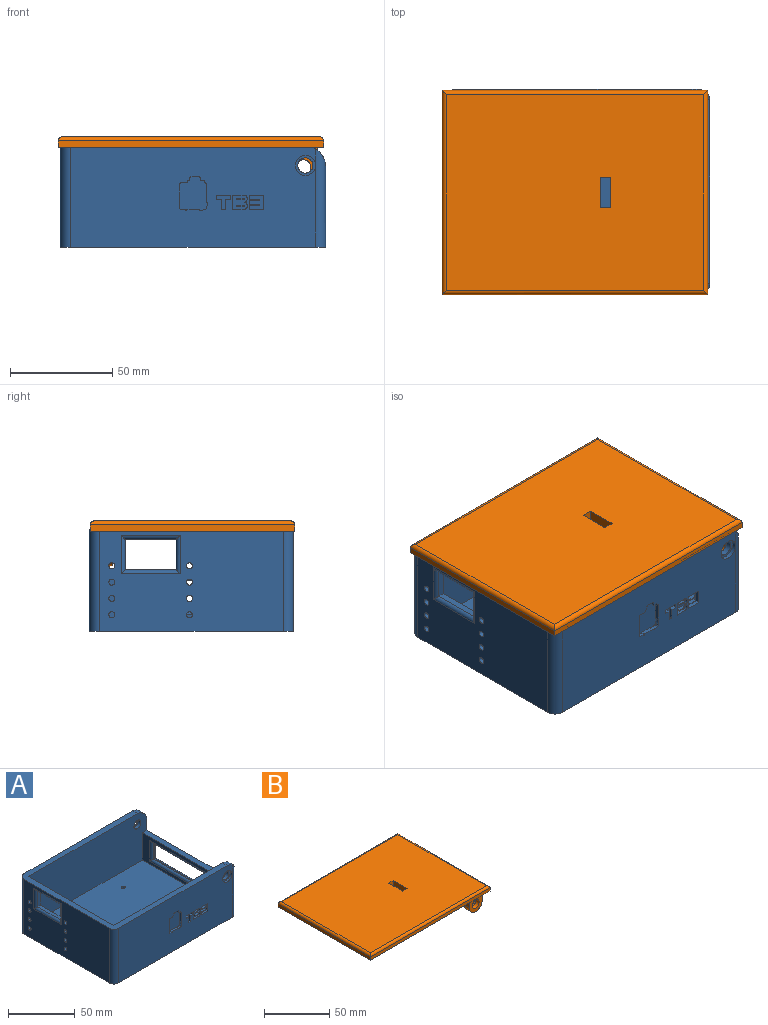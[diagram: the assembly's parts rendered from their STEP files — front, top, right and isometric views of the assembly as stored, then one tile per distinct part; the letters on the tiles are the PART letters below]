
ASSEMBLY  parts=2 mates=1
PART A: 193 faces, bbox 130x100x50 mm
  f0: plane 120x50mm, normal (0,-1,0), area 5613.6mm2, adj f12,f21,f23,f42,f44,f47,f50,f124
  f1: cylinder r=1.5mm len=3mm, axis (-1,0,0), area 28.3mm2, adj f9,f111
  f2: cylinder r=1.5mm len=3mm, axis (-1,0,0), area 28.3mm2, adj f9,f104
  f3: cylinder r=1.5mm len=3mm, axis (-1,0,0), area 28.3mm2, adj f9,f97
  f4: cylinder r=1.5mm len=3mm, axis (-1,0,0), area 28.3mm2, adj f9,f90
  f5: cylinder r=1.5mm len=3mm, axis (-1,0,0), area 28.3mm2, adj f9,f83
  f6: cylinder r=1.5mm len=3mm, axis (-1,0,0), area 28.3mm2, adj f9,f76
  f7: cylinder r=1.5mm len=3mm, axis (-1,0,0), area 28.3mm2, adj f9,f69
  f8: cylinder r=1.5mm len=3mm, axis (-1,0,0), area 28.3mm2, adj f9,f62
  f9: plane 90x50mm, normal (-1,0,0), area 3892.5mm2, adj f1,f2,f3,f4,f5,f6,f7,f8
  f10: plane 90x45mm, normal (1,0,0), area 3502.5mm2, adj f21,f24,f25,f26,f52,f53,f54,f55
  f11: plane 0.67x0.05mm, normal (0,0,1), area 0mm2, adj f12,f24,f47
  f12: cylinder r=11mm len=9.95mm, axis (0,-1,0), area 60.3mm2, adj f0,f11,f24,f42,f47
  f13: cylinder r=3.75mm len=7.5mm, axis (0,-1,0), area 70.7mm2, adj f25,f45
  f14: cylinder r=3.75mm len=7.5mm, axis (0,-1,0), area 70.7mm2, adj f24,f43
  f15: plane 90x25mm, normal (-1,0,0), area 844mm2, adj f24,f25,f26,f51,f116,f117,f118,f119
  f16: cylinder r=1.5mm len=3mm, axis (0,0,1), area 23.6mm2, adj f26,f38
  f17: cylinder r=1.5mm len=3mm, axis (0,0,1), area 23.6mm2, adj f26,f36
  f18: cylinder r=1.5mm len=3mm, axis (0,0,1), area 23.6mm2, adj f26,f34
  f19: cylinder r=1.5mm len=3mm, axis (0,0,1), area 23.6mm2, adj f26,f32
  f20: plane 90x30mm, normal (1,0,0), area 1294mm2, adj f23,f47,f48,f51,f112,f113,f114,f115
  f21: plane 120x100mm, normal (0,0,1), area 1639.3mm2, adj f0,f9,f10,f22,f24,f25,f40,f42
  f22: plane 120x50mm, normal (0,1,0), area 5918mm2, adj f21,f23,f40,f41,f46,f48,f49
  f23: plane 130x100mm, normal (0,0,-1), area 12900mm2, adj f0,f9,f20,f22,f31,f33,f35,f37
  f24: plane 125x45mm, normal (0,1,0), area 5429.9mm2, adj f10,f11,f12,f14,f15,f21,f26,f42
  f25: plane 125x45mm, normal (0,-1,0), area 5429.9mm2, adj f10,f13,f15,f21,f26,f39,f40,f41
  f26: plane 120x90mm, normal (0,0,1), area 10771.7mm2, adj f10,f15,f16,f17,f18,f19,f24,f25
  f27: plane 70x1mm, normal (0,0,1), area 70mm2, adj f28,f30,f115,f116
  f28: plane 15x1mm, normal (0,1,0), area 15mm2, adj f27,f29,f113,f117
  f29: plane 70x1mm, normal (0,0,-1), area 70mm2, adj f28,f30,f112,f119
  f30: plane 15x1mm, normal (0,-1,0), area 15mm2, adj f27,f29,f114,f118
  f31: cylinder r=2.5mm len=5mm, axis (0,0,-1), area 39.3mm2, adj f23,f32
  f32: plane 5x5mm, normal (0,0,-1), area 12.6mm2, adj f19,f31
  f33: cylinder r=2.5mm len=5mm, axis (0,0,-1), area 39.3mm2, adj f23,f34
  f34: plane 5x5mm, normal (0,0,-1), area 12.6mm2, adj f18,f33
  f35: cylinder r=2.5mm len=5mm, axis (0,0,-1), area 39.3mm2, adj f23,f36
  f36: plane 5x5mm, normal (0,0,-1), area 12.6mm2, adj f17,f35
  f37: cylinder r=2.5mm len=5mm, axis (0,0,-1), area 39.3mm2, adj f23,f38
  f38: plane 5x5mm, normal (0,0,-1), area 12.6mm2, adj f16,f37
  f39: plane 0.67x0.05mm, normal (0,0,1), area 0mm2, adj f25,f41,f48
  f40: plane 5x0.05mm, normal (1,0,0), area 0.2mm2, adj f21,f22,f25,f41
  f41: cylinder r=11mm len=9.95mm, axis (0,-1,0), area 60.3mm2, adj f22,f25,f39,f40,f48
  f42: plane 5x0.05mm, normal (1,0,0), area 0.2mm2, adj f0,f12,f21,f24
  f43: plane 10x10mm, normal (0,-1,0), area 34.4mm2, adj f14,f44
  f44: cylinder r=5mm len=10mm, axis (0,-1,0), area 62.8mm2, adj f0,f43
  f45: plane 10x10mm, normal (0,1,0), area 34.4mm2, adj f13,f46
  f46: cylinder r=5mm len=10mm, axis (0,1,0), area 62.8mm2, adj f22,f45
  f47: cylinder r=5mm len=48.22mm, axis (0,0,1), area 347.4mm2, adj f0,f11,f12,f20,f23,f24
  f48: cylinder r=5mm len=48.22mm, axis (0,0,-1), area 347.4mm2, adj f20,f22,f23,f25,f39,f41
  f49: cylinder r=5mm len=50mm, axis (0,0,1), area 392.7mm2, adj f9,f21,f22,f23
  f50: cylinder r=5mm len=50mm, axis (0,0,-1), area 392.7mm2, adj f0,f9,f21,f23
  f51: plane 90x5mm, normal (0,0,1), area 450mm2, adj f15,f20,f24,f25
  f52: plane 25x3mm, normal (0,0,1), area 75mm2, adj f10,f53,f55,f121
  f53: plane 15x3mm, normal (0,1,0), area 45mm2, adj f10,f52,f54,f120
  f54: plane 25x3mm, normal (0,0,-1), area 75mm2, adj f10,f53,f55,f122
  f55: plane 15x3mm, normal (0,-1,0), area 45mm2, adj f10,f52,f54,f123
  f56: plane 2.89x2mm, normal (0,0,1), area 5.8mm2, adj f10,f57,f61,f62
  f57: plane 2.5x2mm, normal (0,-0.87,0.5), area 5.8mm2, adj f10,f56,f58,f62
  f58: plane 2.5x2mm, normal (0,-0.87,-0.5), area 5.8mm2, adj f10,f57,f59,f62
  f59: plane 2.89x2mm, normal (0,0,-1), area 5.8mm2, adj f10,f58,f60,f62
  f60: plane 2.5x2mm, normal (0,0.87,-0.5), area 5.8mm2, adj f10,f59,f61,f62
  f61: plane 2.5x2mm, normal (0,0.87,0.5), area 5.8mm2, adj f10,f56,f60,f62
  f62: plane 5.77x5mm, normal (1,0,0), area 14.6mm2, adj f8,f56,f57,f58,f59,f60,f61
  f63: plane 2.89x2mm, normal (0,0,1), area 5.8mm2, adj f10,f64,f68,f69
  f64: plane 2.5x2mm, normal (0,-0.87,0.5), area 5.8mm2, adj f10,f63,f65,f69
  f65: plane 2.5x2mm, normal (0,-0.87,-0.5), area 5.8mm2, adj f10,f64,f66,f69
  f66: plane 2.89x2mm, normal (0,0,-1), area 5.8mm2, adj f10,f65,f67,f69
  f67: plane 2.5x2mm, normal (0,0.87,-0.5), area 5.8mm2, adj f10,f66,f68,f69
  f68: plane 2.5x2mm, normal (0,0.87,0.5), area 5.8mm2, adj f10,f63,f67,f69
  f69: plane 5.77x5mm, normal (1,0,0), area 14.6mm2, adj f7,f63,f64,f65,f66,f67,f68
  f70: plane 2.5x2mm, normal (0,0.87,-0.5), area 5.8mm2, adj f10,f71,f75,f76
  f71: plane 2.5x2mm, normal (0,0.87,0.5), area 5.8mm2, adj f10,f70,f72,f76
  f72: plane 2.89x2mm, normal (0,0,1), area 5.8mm2, adj f10,f71,f73,f76
  f73: plane 2.5x2mm, normal (0,-0.87,0.5), area 5.8mm2, adj f10,f72,f74,f76
  f74: plane 2.5x2mm, normal (0,-0.87,-0.5), area 5.8mm2, adj f10,f73,f75,f76
  f75: plane 2.89x2mm, normal (0,0,-1), area 5.8mm2, adj f10,f70,f74,f76
  f76: plane 5.77x5mm, normal (1,0,0), area 14.6mm2, adj f6,f70,f71,f72,f73,f74,f75
  f77: plane 2.5x2mm, normal (0,-0.5,0.87), area 5.8mm2, adj f10,f78,f82,f83
  f78: plane 2.89x2mm, normal (0,-1,0), area 5.8mm2, adj f10,f77,f79,f83
  f79: plane 2.5x2mm, normal (0,-0.5,-0.87), area 5.8mm2, adj f10,f78,f80,f83
  f80: plane 2.5x2mm, normal (0,0.5,-0.87), area 5.8mm2, adj f10,f79,f81,f83
  f81: plane 2.89x2mm, normal (0,1,0), area 5.8mm2, adj f10,f80,f82,f83
  f82: plane 2.5x2mm, normal (0,0.5,0.87), area 5.8mm2, adj f10,f77,f81,f83
  f83: plane 5.77x5mm, normal (1,0,0), area 14.6mm2, adj f5,f77,f78,f79,f80,f81,f82
  f84: plane 2.5x2mm, normal (0,0.5,-0.87), area 5.8mm2, adj f10,f85,f89,f90
  f85: plane 2.89x2mm, normal (0,1,0), area 5.8mm2, adj f10,f84,f86,f90
  f86: plane 2.5x2mm, normal (0,0.5,0.87), area 5.8mm2, adj f10,f85,f87,f90
  f87: plane 2.5x2mm, normal (0,-0.5,0.87), area 5.8mm2, adj f10,f86,f88,f90
  f88: plane 2.89x2mm, normal (0,-1,0), area 5.8mm2, adj f10,f87,f89,f90
  f89: plane 2.5x2mm, normal (0,-0.5,-0.87), area 5.8mm2, adj f10,f84,f88,f90
  f90: plane 5.77x5mm, normal (1,0,0), area 14.6mm2, adj f4,f84,f85,f86,f87,f88,f89
  f91: plane 2.5x2mm, normal (0,0.5,-0.87), area 5.8mm2, adj f10,f92,f96,f97
  f92: plane 2.89x2mm, normal (0,1,0), area 5.8mm2, adj f10,f91,f93,f97
  f93: plane 2.5x2mm, normal (0,0.5,0.87), area 5.8mm2, adj f10,f92,f94,f97
  f94: plane 2.5x2mm, normal (0,-0.5,0.87), area 5.8mm2, adj f10,f93,f95,f97
  f95: plane 2.89x2mm, normal (0,-1,0), area 5.8mm2, adj f10,f94,f96,f97
  f96: plane 2.5x2mm, normal (0,-0.5,-0.87), area 5.8mm2, adj f10,f91,f95,f97
  f97: plane 5.77x5mm, normal (1,0,0), area 14.6mm2, adj f3,f91,f92,f93,f94,f95,f96
  f98: plane 2.46x2mm, normal (0,0.5,-0.87), area 5.7mm2, adj f10,f99,f103,f104
  f99: plane 2.84x2mm, normal (0,1,0), area 5.7mm2, adj f10,f98,f100,f104
  f100: plane 2.46x2mm, normal (0,0.5,0.87), area 5.7mm2, adj f10,f99,f101,f104
  f101: plane 2.46x2mm, normal (0,-0.5,0.87), area 5.7mm2, adj f10,f100,f102,f104
  f102: plane 2.84x2mm, normal (0,-1,0), area 5.7mm2, adj f10,f101,f103,f104
  f103: plane 2.46x2mm, normal (0,-0.5,-0.87), area 5.7mm2, adj f10,f98,f102,f104
  f104: plane 5.68x4.92mm, normal (1,0,0), area 13.9mm2, adj f2,f98,f99,f100,f101,f102,f103
  f105: plane 2.5x2mm, normal (0,0.5,-0.87), area 5.8mm2, adj f10,f106,f110,f111
  f106: plane 2.89x2mm, normal (0,1,0), area 5.8mm2, adj f10,f105,f107,f111
  f107: plane 2.5x2mm, normal (0,0.5,0.87), area 5.8mm2, adj f10,f106,f108,f111
  f108: plane 2.5x2mm, normal (0,-0.5,0.87), area 5.8mm2, adj f10,f107,f109,f111
  f109: plane 2.89x2mm, normal (0,-1,0), area 5.8mm2, adj f10,f108,f110,f111
  f110: plane 2.5x2mm, normal (0,-0.5,-0.87), area 5.8mm2, adj f10,f105,f109,f111
  f111: plane 5.77x5mm, normal (1,0,0), area 14.6mm2, adj f1,f105,f106,f107,f108,f109,f110
  f112: cylinder r=2mm len=74mm, axis (0,1,0), area 224.5mm2, adj f20,f29,f113,f114
  f113: cylinder r=2mm len=19mm, axis (0,0,1), area 51.7mm2, adj f20,f28,f112,f115
  f114: cylinder r=2mm len=19mm, axis (0,0,-1), area 51.7mm2, adj f20,f30,f112,f115
  f115: cylinder r=2mm len=74mm, axis (0,-1,0), area 224.5mm2, adj f20,f27,f113,f114
  f116: cylinder r=2mm len=74mm, axis (0,-1,0), area 224.5mm2, adj f15,f27,f117,f118
  f117: cylinder r=2mm len=19mm, axis (0,0,1), area 51.7mm2, adj f15,f28,f116,f119
  f118: cylinder r=2mm len=19mm, axis (0,0,-1), area 51.7mm2, adj f15,f30,f116,f119
  f119: cylinder r=2mm len=74mm, axis (0,1,0), area 224.5mm2, adj f15,f29,f117,f118
  f120: cylinder r=2mm len=19mm, axis (0,0,-1), area 51.7mm2, adj f9,f53,f121,f122
  f121: cylinder r=2mm len=29mm, axis (0,1,0), area 83.1mm2, adj f9,f52,f120,f123
  f122: cylinder r=2mm len=29mm, axis (0,-1,0), area 83.1mm2, adj f9,f54,f120,f123
  f123: cylinder r=2mm len=19mm, axis (0,0,1), area 51.7mm2, adj f9,f55,f121,f122
  f124: plane 7x2mm, normal (0,0,-1), area 14mm2, adj f0,f125,f131,f132
  f125: plane 2x2mm, normal (1,0,0), area 4mm2, adj f0,f124,f126,f132
  f126: plane 2.5x2mm, normal (0,0,1), area 5mm2, adj f0,f125,f127,f132
  f127: plane 5x2mm, normal (1,0,0), area 10mm2, adj f0,f126,f128,f132
  f128: plane 2x2mm, normal (0,0,1), area 4mm2, adj f0,f127,f129,f132
  f129: plane 5x2mm, normal (-1,0,0), area 10mm2, adj f0,f128,f130,f132
  f130: plane 2.5x2mm, normal (0,0,1), area 5mm2, adj f0,f129,f131,f132
  f131: plane 2x2mm, normal (-1,0,0), area 4mm2, adj f0,f124,f130,f132
  f132: plane 7x7mm, normal (0,-1,0), area 24mm2, adj f124,f125,f126,f127,f128,f129,f130,f131
  f133: plane 2x2mm, normal (1,0,0), area 4mm2, adj f0,f134,f144,f145
  f134: plane 7x2mm, normal (0,0,1), area 14mm2, adj f0,f133,f135,f145
  f135: plane 7x2mm, normal (-1,0,0), area 14mm2, adj f0,f134,f136,f145
  f136: plane 7x2mm, normal (0,0,-1), area 14mm2, adj f0,f135,f137,f145
  f137: plane 2x2mm, normal (1,0,0), area 4mm2, adj f0,f136,f138,f145
  f138: plane 4.75x2mm, normal (0,0,1), area 9.5mm2, adj f0,f137,f139,f145
  f139: cylinder r=0.25mm len=2mm, axis (0,-1,0), area 1.6mm2, adj f0,f138,f140,f145
  f140: plane 4.75x2mm, normal (0,0,-1), area 9.5mm2, adj f0,f139,f141,f145
  f141: plane 2x2mm, normal (1,0,0), area 4mm2, adj f0,f140,f142,f145
  f142: plane 4.75x2mm, normal (0,0,1), area 9.5mm2, adj f0,f141,f143,f145
  f143: cylinder r=0.25mm len=2mm, axis (0,-1,0), area 1.6mm2, adj f0,f142,f144,f145
  f144: plane 4.75x2mm, normal (0,0,-1), area 9.5mm2, adj f0,f133,f143,f145
  f145: plane 7x7mm, normal (0,-1,0), area 44.1mm2, adj f133,f134,f135,f136,f137,f138,f139,f140
  f146: plane 3.5x2mm, normal (0,0,-1), area 7mm2, adj f147,f162,f163,f192
  f147: plane 2x0.5mm, normal (-1,0,0), area 1mm2, adj f146,f148,f163,f192
  f148: plane 3.5x2mm, normal (0,0,1), area 7mm2, adj f147,f162,f163,f192
  f149: plane 7x2mm, normal (1,0,0), area 14mm2, adj f0,f150,f160,f163
  f150: plane 5.5x2mm, normal (0,0,1), area 11mm2, adj f0,f149,f151,f163
  f151: cylinder r=1.5mm len=2mm, axis (0,-1,0), area 4.7mm2, adj f0,f150,f152,f163
  f152: plane 2x0.5mm, normal (-1,0,0), area 1mm2, adj f0,f151,f153,f163
  f153: cylinder r=1.5mm len=2mm, axis (0,-1,0), area 4.7mm2, adj f0,f152,f154,f163
  f154: cylinder r=1.5mm len=2mm, axis (0,-1,0), area 4.7mm2, adj f0,f153,f155,f163
  f155: plane 2x0.5mm, normal (-1,0,0), area 1mm2, adj f0,f154,f156,f163
  f156: cylinder r=1.5mm len=2mm, axis (0,-1,0), area 4.7mm2, adj f0,f155,f160,f163
  f157: plane 2x0.5mm, normal (-1,0,0), area 1mm2, adj f158,f161,f163,f164
  f158: plane 3.5x2mm, normal (0,0,1), area 7mm2, adj f157,f159,f163,f164
  f159: plane 2x0.5mm, normal (1,0,0), area 1mm2, adj f158,f161,f163,f164
  f160: plane 5.5x2mm, normal (0,0,-1), area 11mm2, adj f0,f149,f156,f163
  f161: plane 3.5x2mm, normal (0,0,-1), area 7mm2, adj f157,f159,f163,f164
  f162: plane 2x0.5mm, normal (1,0,0), area 1mm2, adj f146,f148,f163,f192
  f163: plane 7x7mm, normal (0,-1,0), area 43.6mm2, adj f146,f147,f148,f149,f150,f151,f152,f153
  f164: plane 3.5x0.5mm, normal (0,-1,0), area 1.8mm2, adj f157,f158,f159,f161
  f165: cylinder r=3mm len=3.32mm, axis (0,-1,0), area 7mm2, adj f0,f166,f190,f191
  f166: plane 8.34x2mm, normal (-1,0,0), area 16.7mm2, adj f0,f165,f167,f191
  f167: cylinder r=0.5mm len=2mm, axis (0,-1,0), area 1.6mm2, adj f0,f166,f168,f191
  f168: plane 2x0.5mm, normal (0,0,-1), area 1mm2, adj f0,f167,f169,f191
  f169: plane 2x0.8mm, normal (-1,0,0), area 1.6mm2, adj f0,f168,f170,f191
  f170: cylinder r=0.2mm len=2mm, axis (0,-1,0), area 0.6mm2, adj f0,f169,f171,f191
  f171: plane 2x1.8mm, normal (0,0,-1), area 3.6mm2, adj f0,f170,f172,f191
  f172: plane 2x1.5mm, normal (-1,0,0), area 3mm2, adj f0,f171,f173,f191
  f173: cylinder r=0.5mm len=2mm, axis (0,-1,0), area 1.6mm2, adj f0,f172,f174,f191
  f174: plane 4x2mm, normal (0,0,-1), area 8mm2, adj f0,f173,f175,f191
  f175: cylinder r=0.5mm len=2mm, axis (0,-1,0), area 1.6mm2, adj f0,f174,f176,f191
  f176: plane 2x1.5mm, normal (1,0,0), area 3mm2, adj f0,f175,f177,f191
  f177: plane 2x0.8mm, normal (0,0,-1), area 1.6mm2, adj f0,f176,f178,f191
  f178: cylinder r=0.2mm len=2mm, axis (0,-1,0), area 0.6mm2, adj f0,f177,f179,f191
  f179: plane 2x0.8mm, normal (1,0,0), area 1.6mm2, adj f0,f178,f180,f191
  f180: plane 3.5x2mm, normal (0,0,-1), area 7mm2, adj f0,f179,f181,f191
  f181: cylinder r=0.5mm len=2mm, axis (0,-1,0), area 1.6mm2, adj f0,f180,f182,f191
  f182: plane 12x2mm, normal (1,0,0), area 24mm2, adj f0,f181,f183,f191
  f183: cylinder r=0.5mm len=2mm, axis (0,-1,0), area 1.6mm2, adj f0,f182,f184,f191
  f184: plane 2x2mm, normal (0,0,1), area 4mm2, adj f0,f183,f185,f191
  f185: cylinder r=0.5mm len=2mm, axis (0,-1,0), area 3.1mm2, adj f0,f184,f186,f191
  f186: plane 5.34x2mm, normal (0,0,1), area 10.7mm2, adj f0,f185,f187,f191
  f187: cylinder r=3mm len=3.32mm, axis (0,-1,0), area 7mm2, adj f0,f186,f188,f191
  f188: plane 2x0.34mm, normal (0,0,1), area 0.7mm2, adj f0,f187,f189,f191
  f189: cylinder r=0.5mm len=2mm, axis (0,-1,0), area 1.6mm2, adj f0,f188,f190,f191
  f190: plane 2x0.34mm, normal (-1,0,0), area 0.7mm2, adj f0,f165,f189,f191
  f191: plane 16.5x13.5mm, normal (0,-1,0), area 189.3mm2, adj f165,f166,f167,f168,f169,f170,f171,f172
  f192: plane 3.5x0.5mm, normal (0,-1,0), area 1.8mm2, adj f146,f147,f148,f162
PART B: 30 faces, bbox 130x100x22 mm
  f0: plane 126x96mm, normal (0,0,1), area 12021mm2, adj f22,f23,f24,f25,f26,f27,f28,f29
  f1: plane 130x100mm, normal (0,0,-1), area 12771mm2, adj f4,f5,f6,f7,f8,f9,f10,f11
  f2: cylinder r=3.75mm len=7.5mm, axis (0,-1,0), area 82.5mm2, adj f6,f20
  f3: cylinder r=3.75mm len=7.5mm, axis (0,-1,0), area 82.5mm2, adj f4,f18
  f4: plane 17x14mm, normal (0,-1,0), area 172.8mm2, adj f1,f3,f14,f15,f17
  f5: plane 17x14mm, normal (0,1,0), area 153.4mm2, adj f1,f14,f15,f17,f19
  f6: plane 17x14mm, normal (0,1,0), area 172.8mm2, adj f1,f2,f8,f9,f16
  f7: plane 17x14mm, normal (0,-1,0), area 153.4mm2, adj f1,f8,f9,f16,f21
  f8: plane 10x5.5mm, normal (-1,0,0), area 55mm2, adj f1,f6,f7,f16
  f9: plane 10x5.5mm, normal (1,0,0), area 55mm2, adj f1,f6,f7,f16
  f10: plane 130x3mm, normal (0,-1,0), area 390mm2, adj f1,f11,f13,f26
  f11: plane 100x3mm, normal (1,0,0), area 300mm2, adj f1,f10,f12,f27
  f12: plane 130x3mm, normal (0,1,0), area 390mm2, adj f1,f11,f13,f29
  f13: plane 100x3mm, normal (-1,0,0), area 300mm2, adj f1,f10,f12,f28
  f14: plane 10x5.5mm, normal (-1,0,0), area 55mm2, adj f1,f4,f5,f17
  f15: plane 10x5.5mm, normal (1,0,0), area 55mm2, adj f1,f4,f5,f17
  f16: cylinder r=7mm len=14mm, axis (0,-1,0), area 121mm2, adj f6,f7,f8,f9
  f17: cylinder r=7mm len=14mm, axis (0,-1,0), area 121mm2, adj f4,f5,f14,f15
  f18: plane 9x9mm, normal (0,1,0), area 19.4mm2, adj f3,f19
  f19: cylinder r=4.5mm len=9mm, axis (0,1,0), area 56.5mm2, adj f5,f18
  f20: plane 9x9mm, normal (0,-1,0), area 19.4mm2, adj f2,f21
  f21: cylinder r=4.5mm len=9mm, axis (0,-1,0), area 56.5mm2, adj f7,f20
  f22: plane 5x5mm, normal (0,1,0), area 25mm2, adj f0,f1,f23,f25
  f23: plane 15x5mm, normal (-1,0,0), area 75mm2, adj f0,f1,f22,f24
  f24: plane 5x5mm, normal (0,-1,0), area 25mm2, adj f0,f1,f23,f25
  f25: plane 15x5mm, normal (1,0,0), area 75mm2, adj f0,f1,f22,f24
  f26: cylinder r=2mm len=130mm, axis (-1,0,0), area 403.8mm2, adj f0,f10,f27,f28
  f27: cylinder r=2mm len=100mm, axis (0,-1,0), area 309.6mm2, adj f0,f11,f26,f29
  f28: cylinder r=2mm len=100mm, axis (0,1,0), area 309.6mm2, adj f0,f13,f26,f29
  f29: cylinder r=2mm len=130mm, axis (1,0,0), area 403.8mm2, adj f0,f12,f27,f28
PLACE A at identity fixed
PLACE B t=(-1,-0.5,49)mm
MATE cylindrical B.f2 <-> A.f12  axis (0,1,0) through (54,44,39)mm
